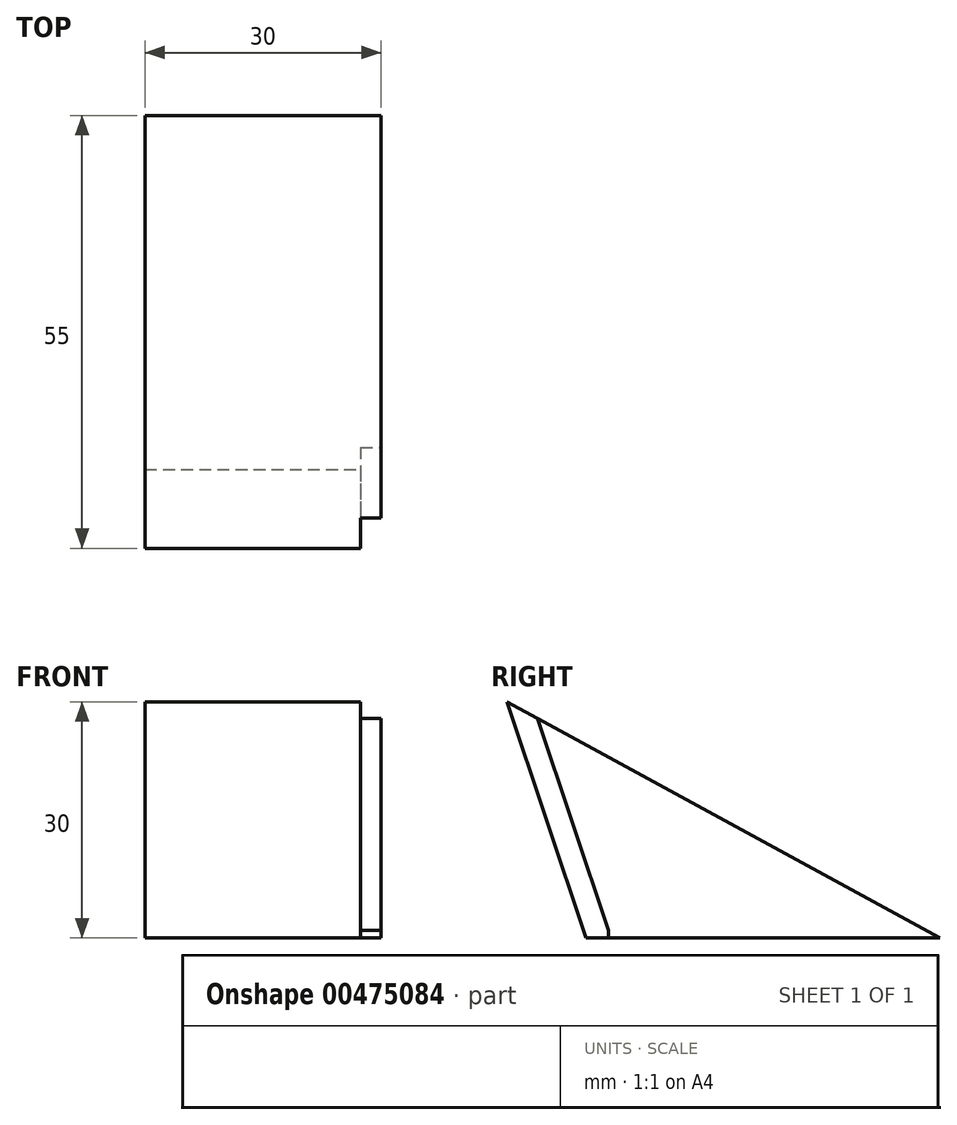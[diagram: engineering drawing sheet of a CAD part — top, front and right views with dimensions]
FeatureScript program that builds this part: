
annotation { "Feature Type Name" : "Feature", "Feature Type Description" : "" }
export const myFeature = defineFeature(function(context is Context, id is Id, definition is map)
    precondition{}
    {
        {
            var Q0;
            Q0=qCreatedBy(makeId("Top.planeOp"),FACE);
            var sketch = newSketch(context, id + "F0", { "sketchPlane" : qUnion([Q0])});
            skLineSegment(sketch, "E0.bottom", {"start": v(-15, 22.5) * mm, "end": v(15, 22.5) * mm});
            skLineSegment(sketch, "E0.top", {"start": v(-15, -22.5) * mm, "end": v(15, -22.5) * mm});
            skLineSegment(sketch, "E0.left", {"start": v(-15, 22.5) * mm, "end": v(-15, -22.5) * mm});
            skLineSegment(sketch, "E0.right", {"start": v(15, 22.5) * mm, "end": v(15, -22.5) * mm});
            skPoint(sketch, "E0.middle", {"position": v(0, 0) * mm});
            skLineSegment(sketch, "E1", {"start": v(15, -22.5) * mm, "end": v(15, -32.5) * mm});
            skLineSegment(sketch, "E2", {"start": v(15, -32.5) * mm, "end": v(-15, -32.5) * mm});
            skLineSegment(sketch, "E3", {"start": v(-15, -32.5) * mm, "end": v(-15, -22.5) * mm});
            skSolve(sketch);
        }
        {
            var Q0;
            Q0=makeQuery(id+"F0.imprint","IMPRINT",FACE,{"disambiguationData":[TD([[makeQuery(id+"F0.imprint","IMPRINT",EDGE,{"derivedFrom":sQuery(id+"F0.wireOp",EDGE,"E0.bottom")}),-1.0]])]});
            var Q1;
            Q1=makeQuery(id+"F0.imprint","IMPRINT",FACE,{"disambiguationData":[TD([[makeQuery(id+"F0.imprint","IMPRINT",EDGE,{"derivedFrom":sQuery(id+"F0.wireOp",EDGE,"E0.top")}),-1.0]])]});
            extrude(context, id + "F1", {"entities" : qUnion([Q0, Q1]), "depth" : 30 * mm});
        }
        {
            var Q0;
            Q0=makeQuery(id+"F1.opExtrude","SWEPT_FACE",FACE,{"disambiguationData":[OSD([sQuery(id+"F0.wireOp",EDGE,"E0.right"),sQuery(id+"F0.wireOp",EDGE,"E1")])]});
            var sketch = newSketch(context, id + "F2", { "sketchPlane" : qUnion([Q0])});
            skLineSegment(sketch, "E4.0", {"start": v(-22.5, 0) * mm, "end": v(-32.5, 0) * mm});
            skLineSegment(sketch, "E5", {"start": v(-22.5, 0) * mm, "end": v(-32.5, 30) * mm});
            skLineSegment(sketch, "E6", {"start": v(-32.5, 30) * mm, "end": v(22.5, 0) * mm});
            skLineSegment(sketch, "E7", {"start": v(0, 0) * mm, "end": v(-5, 0) * mm});
            skLineSegment(sketch, "E8", {"start": v(0, 0) * mm, "end": v(5, 0) * mm});
            skLineSegment(sketch, "E9", {"start": v(-5, 0) * mm, "end": v(-5, 6) * mm});
            skLineSegment(sketch, "E10", {"start": v(-5, 6) * mm, "end": v(5, 6) * mm});
            skLineSegment(sketch, "E11", {"start": v(5, 6) * mm, "end": v(5, 0) * mm});
            skSolve(sketch);
        }
        {
            var Q0;
            Q0=makeQuery(id+"F2.imprint","IMPRINT",FACE,{"disambiguationData":[TD([[makeQuery(id+"F2.imprint","IMPRINT",EDGE,{"derivedFrom":sQuery(id+"F2.wireOp",EDGE,"E4.0")}),-1.0]])]});
            var Q1;
            Q1=makeQuery(id+"F2.imprint","IMPRINT",FACE,{"disambiguationData":[TD([[makeQuery(id+"F2.imprint","IMPRINT",EDGE,{"derivedFrom":sQuery(id+"F2.wireOp",EDGE,"E6")}),1.0]])]});
            extrude(context, id + "F3", {"entities" : qUnion([Q0, Q1]), "operationType" : NewBodyOperationType.REMOVE, "endBound" : BoundingType.THROUGH_ALL, "oppositeDirection" : true, "depth" : 25 * mm});
        }
        {
            var Q0;
            Q0=makeQuery(id+"F3.boolean.opBoolean","COPY",FACE,{"derivedFrom":makeQuery(id+"F3.opExtrude","SWEPT_FACE",FACE,{"disambiguationData":[OSD([sQuery(id+"F2.wireOp",EDGE,"E5")])]})});
            var sketch = newSketch(context, id + "F4", { "sketchPlane" : qUnion([Q0])});
            skLineSegment(sketch, "E12", {"start": v(15, 7.12) * mm, "end": v(12.4, 7.12) * mm});
            skLineSegment(sketch, "E13", {"start": v(12.4, 7.12) * mm, "end": v(12.4, 38.74) * mm});
            skSolve(sketch);
        }
        {
            var Q0;
            Q0=makeQuery(id+"F4.imprint","IMPRINT",FACE,{"disambiguationData":[TD([[makeQuery(id+"F4.imprint","IMPRINT",EDGE,{"derivedFrom":sQuery(id+"F4.wireOp",EDGE,"E12")}),1.0]])]});
            extrude(context, id + "F5", {"entities" : qUnion([Q0]), "operationType" : NewBodyOperationType.REMOVE, "oppositeDirection" : true, "depth" : 3 * mm});
        }
        {
            var Q0;
            Q0=makeQuery(id+"F1.opExtrude","SWEPT_FACE",FACE,{"disambiguationData":[OSD([sQuery(id+"F0.wireOp",EDGE,"E0.right"),sQuery(id+"F0.wireOp",EDGE,"E1")])]});
            var sketch = newSketch(context, id + "F6", { "sketchPlane" : qUnion([Q0])});
            skLineSegment(sketch, "E14", {"start": v(-19.65, 0.95) * mm, "end": v(-19.65, 0) * mm});
            skSolve(sketch);
        }
        {
            var Q0;
            {var subQ0=sQuery(id+"F6.wireOp",EDGE,"E14");Q0=makeQuery(id+"F6.imprint","IMPRINT",FACE,{"disambiguationData":[TD([[makeQuery(id+"F6.imprint","IMPRINT",EDGE,{"derivedFrom":subQ0}),-1.0]])]});}
            extrude(context, id + "F7", {"entities" : qUnion([Q0]), "operationType" : NewBodyOperationType.REMOVE, "oppositeDirection" : true, "depth" : 2.6 * mm});
        }
    });
